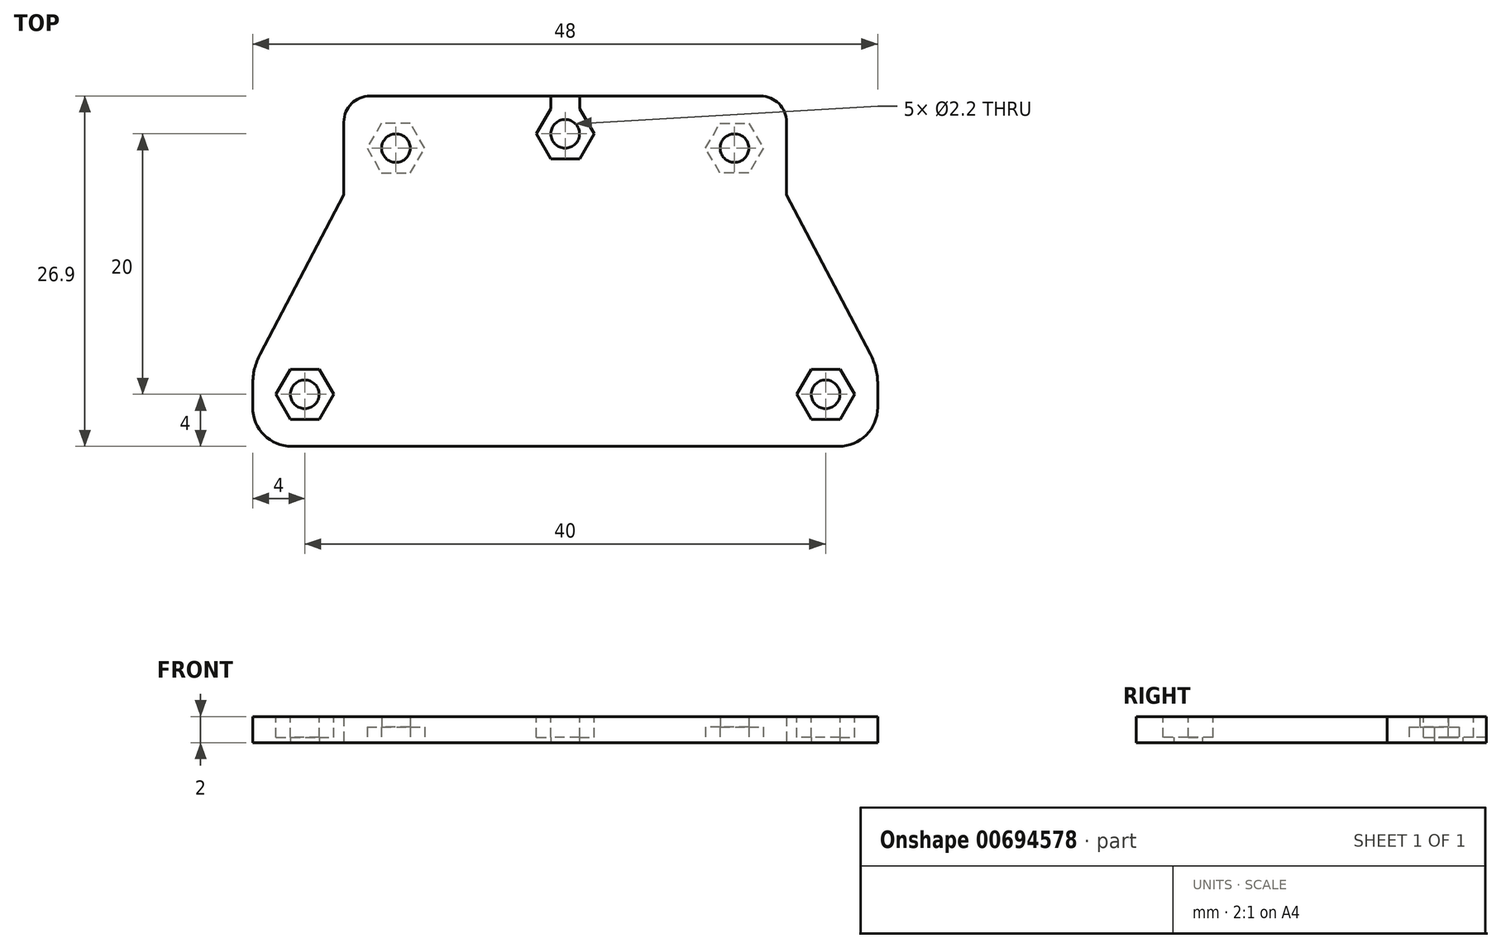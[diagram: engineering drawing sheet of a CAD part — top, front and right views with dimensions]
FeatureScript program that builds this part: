
annotation { "Feature Type Name" : "Feature", "Feature Type Description" : "" }
export const myFeature = defineFeature(function(context is Context, id is Id, definition is map)
    precondition{}
    {
        {
            var Q0;
            Q0=qCreatedBy(makeId("Top.planeOp"),FACE);
            var sketch = newSketch(context, id + "F0", { "sketchPlane" : qUnion([Q0])});
            skCircle(sketch, "E0", {"center": v(-13, 0) * mm, "radius": 1.1 * mm});
            skCircle(sketch, "E1", {"center": v(0, 1.1) * mm, "radius": 1.1 * mm});
            skCircle(sketch, "E2", {"center": v(-20, -18.9) * mm, "radius": 1.1 * mm});
            skCircle(sketch, "E3.MirrorC", {"center": v(20, -18.9) * mm, "radius": 1.1 * mm});
            skCircle(sketch, "E4.MirrorC", {"center": v(13, 0) * mm, "radius": 1.1 * mm});
            skLineSegment(sketch, "E5", {"start": v(-14.82, 3.1) * mm, "end": v(20.83, 3.1) * mm, "construction": true});
            skSolve(sketch);
        }
        {
            var Q0;
            Q0=qCreatedBy(makeId("Top.planeOp"),FACE);
            var sketch = newSketch(context, id + "F1", { "sketchPlane" : qUnion([Q0])});
            skLineSegment(sketch, "E6", {"start": v(-3, 4) * mm, "end": v(-13, 4) * mm});
            skLineSegment(sketch, "E7", {"start": v(-17, -3.6) * mm, "end": v(-24, -16.9) * mm});
            skLineSegment(sketch, "E8", {"start": v(-24, -22.9) * mm, "end": v(0, -22.9) * mm});
            skLineSegment(sketch, "E9", {"start": v(-3, 4) * mm, "end": v(0, 4) * mm});
            skLineSegment(sketch, "E10", {"start": v(-13, 4) * mm, "end": v(-17, 4) * mm});
            skLineSegment(sketch, "E11", {"start": v(-17, 4) * mm, "end": v(-17, -3.6) * mm});
            skLineSegment(sketch, "E12", {"start": v(-24, -16.9) * mm, "end": v(-24, -22.9) * mm});
            skLineSegment(sketch, "E13.MirrorCS", {"start": v(24, -22.9) * mm, "end": v(0, -22.9) * mm});
            skLineSegment(sketch, "E14.MirrorCS", {"start": v(17, -3.6) * mm, "end": v(24, -16.9) * mm});
            skLineSegment(sketch, "E15.MirrorCS", {"start": v(24, -16.9) * mm, "end": v(24, -22.9) * mm});
            skLineSegment(sketch, "E16.MirrorCS", {"start": v(3, 4) * mm, "end": v(0, 4) * mm});
            skLineSegment(sketch, "E17.MirrorCS", {"start": v(13, 4) * mm, "end": v(17, 4) * mm});
            skLineSegment(sketch, "E18.MirrorCS", {"start": v(3, 4) * mm, "end": v(13, 4) * mm});
            skLineSegment(sketch, "E19.MirrorCS", {"start": v(17, 4) * mm, "end": v(17, -3.6) * mm});
            skSolve(sketch);
        }
        {
            var Q0;
            Q0 = qSketchRegion(id + "F1", true);
            extrude(context, id + "F2", {"entities" : qUnion([Q0]), "depth" : 2 * mm, "offsetDistance" : 25 * mm});
        }
        {
            var Q0;
            Q0=makeQuery(id+"F2.opExtrude","CAP_FACE",FACE,{"disambiguationData":[OSD([sQuery(id+"F1.wireOp",EDGE,"E6"),sQuery(id+"F1.wireOp",EDGE,"E7"),sQuery(id+"F1.wireOp",EDGE,"E8"),sQuery(id+"F1.wireOp",EDGE,"E9"),sQuery(id+"F1.wireOp",EDGE,"E10"),sQuery(id+"F1.wireOp",EDGE,"E11"),sQuery(id+"F1.wireOp",EDGE,"E12"),sQuery(id+"F1.wireOp",EDGE,"E13.MirrorCS"),sQuery(id+"F1.wireOp",EDGE,"E14.MirrorCS"),sQuery(id+"F1.wireOp",EDGE,"E15.MirrorCS"),sQuery(id+"F1.wireOp",EDGE,"E16.MirrorCS"),sQuery(id+"F1.wireOp",EDGE,"E17.MirrorCS"),sQuery(id+"F1.wireOp",EDGE,"E18.MirrorCS"),sQuery(id+"F1.wireOp",EDGE,"E19.MirrorCS")])],"isStart":true});
            var sketch = newSketch(context, id + "F3", { "sketchPlane" : qUnion([Q0])});
            skCircle(sketch, "E20", {"center": v(20, 18.9) * mm, "radius": 1.1 * mm});
            skCircle(sketch, "E21", {"center": v(13, 0) * mm, "radius": 1.1 * mm});
            skCircle(sketch, "E22", {"center": v(0, -1.1) * mm, "radius": 1.1 * mm});
            skCircle(sketch, "E23", {"center": v(-13, 0) * mm, "radius": 1.1 * mm});
            skCircle(sketch, "E24", {"center": v(-20, 18.9) * mm, "radius": 1.1 * mm});
            skSolve(sketch);
        }
        {
            var Q0;
            Q0 = qSketchRegion(id + "F3", true);
            extrude(context, id + "F4", {"entities" : qUnion([Q0]), "operationType" : NewBodyOperationType.REMOVE, "endBound" : BoundingType.UP_TO_NEXT, "oppositeDirection" : true, "depth" : 25 * mm, "offsetDistance" : 25 * mm});
        }
        {
            var Q0;
            Q0=qCreatedBy(makeId("Top.planeOp"),FACE);
            var sketch = newSketch(context, id + "F5", { "sketchPlane" : qUnion([Q0])});
            skCircle(sketch, "E25.cCircle", {"center": v(13, 0) * mm, "radius": 1.92 * mm, "construction": true});
            skLineSegment(sketch, "E25.0", {"start": v(11.9, -1.92) * mm, "end": v(10.78, 0) * mm});
            skLineSegment(sketch, "E25.1", {"start": v(10.78, 0) * mm, "end": v(11.9, 1.92) * mm});
            skLineSegment(sketch, "E25.2", {"start": v(11.9, 1.92) * mm, "end": v(14.1, 1.92) * mm});
            skLineSegment(sketch, "E25.3", {"start": v(14.1, 1.92) * mm, "end": v(15.22, 0) * mm});
            skLineSegment(sketch, "E25.4", {"start": v(15.22, 0) * mm, "end": v(14.1, -1.92) * mm});
            skLineSegment(sketch, "E25.5", {"start": v(14.1, -1.92) * mm, "end": v(11.9, -1.92) * mm});
            skPoint(sketch, "E25.0.midPoint", {"position": v(11.34, -0.96) * mm});
            skLineSegment(sketch, "E26.MirrorCS", {"start": v(-11.9, -1.92) * mm, "end": v(-10.78, 0) * mm});
            skLineSegment(sketch, "E27.MirrorCS", {"start": v(-14.1, 1.92) * mm, "end": v(-15.22, 0) * mm});
            skPoint(sketch, "E28.MirrorP", {"position": v(-11.34, -0.96) * mm});
            skCircle(sketch, "E29.MirrorC", {"center": v(-13, 0) * mm, "radius": 1.92 * mm, "construction": true});
            skLineSegment(sketch, "E30.MirrorCS", {"start": v(-10.78, 0) * mm, "end": v(-11.9, 1.92) * mm});
            skLineSegment(sketch, "E31.MirrorCS", {"start": v(-11.9, 1.92) * mm, "end": v(-14.1, 1.92) * mm});
            skLineSegment(sketch, "E32.MirrorCS", {"start": v(-15.22, 0) * mm, "end": v(-14.1, -1.92) * mm});
            skLineSegment(sketch, "E33.MirrorCS", {"start": v(-14.1, -1.92) * mm, "end": v(-11.9, -1.92) * mm});
            skSolve(sketch);
        }
        {
            var Q0;
            Q0 = qSketchRegion(id + "F5", true);
            extrude(context, id + "F6", {"entities" : qUnion([Q0]), "operationType" : NewBodyOperationType.REMOVE, "depth" : 1.2 * mm, "offsetDistance" : 25 * mm});
        }
        {
            var Q0;
            Q0=makeQuery(id+"F2.opExtrude","CAP_FACE",FACE,{"disambiguationData":[OSD([sQuery(id+"F1.wireOp",EDGE,"E6"),sQuery(id+"F1.wireOp",EDGE,"E7"),sQuery(id+"F1.wireOp",EDGE,"E8"),sQuery(id+"F1.wireOp",EDGE,"E9"),sQuery(id+"F1.wireOp",EDGE,"E10"),sQuery(id+"F1.wireOp",EDGE,"E11"),sQuery(id+"F1.wireOp",EDGE,"E12"),sQuery(id+"F1.wireOp",EDGE,"E13.MirrorCS"),sQuery(id+"F1.wireOp",EDGE,"E14.MirrorCS"),sQuery(id+"F1.wireOp",EDGE,"E15.MirrorCS"),sQuery(id+"F1.wireOp",EDGE,"E16.MirrorCS"),sQuery(id+"F1.wireOp",EDGE,"E17.MirrorCS"),sQuery(id+"F1.wireOp",EDGE,"E18.MirrorCS"),sQuery(id+"F1.wireOp",EDGE,"E19.MirrorCS")])],"isStart":false});
            var sketch = newSketch(context, id + "F7", { "sketchPlane" : qUnion([Q0])});
            skCircle(sketch, "E34.cCircle", {"center": v(-20, -18.9) * mm, "radius": 1.92 * mm, "construction": true});
            skLineSegment(sketch, "E34.0", {"start": v(-18.9, -16.98) * mm, "end": v(-17.78, -18.9) * mm});
            skLineSegment(sketch, "E34.1", {"start": v(-17.78, -18.9) * mm, "end": v(-18.9, -20.82) * mm});
            skLineSegment(sketch, "E34.2", {"start": v(-18.9, -20.82) * mm, "end": v(-21.1, -20.82) * mm});
            skLineSegment(sketch, "E34.3", {"start": v(-21.1, -20.82) * mm, "end": v(-22.22, -18.9) * mm});
            skLineSegment(sketch, "E34.4", {"start": v(-22.22, -18.9) * mm, "end": v(-21.1, -16.98) * mm});
            skLineSegment(sketch, "E34.5", {"start": v(-21.1, -16.98) * mm, "end": v(-18.9, -16.98) * mm});
            skPoint(sketch, "E34.0.midPoint", {"position": v(-18.34, -17.94) * mm});
            skCircle(sketch, "E35.cCircle", {"center": v(0, 1.1) * mm, "radius": 1.92 * mm, "construction": true});
            skLineSegment(sketch, "E35.0", {"start": v(-1.1, 3.02) * mm, "end": v(1.1, 3.02) * mm});
            skLineSegment(sketch, "E35.1", {"start": v(1.1, 3.02) * mm, "end": v(2.22, 1.1) * mm});
            skLineSegment(sketch, "E35.2", {"start": v(2.22, 1.1) * mm, "end": v(1.1, -0.82) * mm});
            skLineSegment(sketch, "E35.3", {"start": v(1.1, -0.82) * mm, "end": v(-1.1, -0.82) * mm});
            skLineSegment(sketch, "E35.4", {"start": v(-1.1, -0.82) * mm, "end": v(-2.22, 1.1) * mm});
            skLineSegment(sketch, "E35.5", {"start": v(-2.22, 1.1) * mm, "end": v(-1.1, 3.02) * mm});
            skPoint(sketch, "E35.0.midPoint", {"position": v(0, 3.02) * mm});
            skLineSegment(sketch, "E36.MirrorCS", {"start": v(17.78, -18.9) * mm, "end": v(18.9, -20.82) * mm});
            skLineSegment(sketch, "E37.MirrorCS", {"start": v(22.22, -18.9) * mm, "end": v(21.1, -16.98) * mm});
            skLineSegment(sketch, "E38.MirrorCS", {"start": v(18.9, -16.98) * mm, "end": v(17.78, -18.9) * mm});
            skLineSegment(sketch, "E39.MirrorCS", {"start": v(21.1, -20.82) * mm, "end": v(22.22, -18.9) * mm});
            skLineSegment(sketch, "E40.MirrorCS", {"start": v(21.1, -16.98) * mm, "end": v(18.9, -16.98) * mm});
            skCircle(sketch, "E41.MirrorC", {"center": v(20, -18.9) * mm, "radius": 1.92 * mm, "construction": true});
            skLineSegment(sketch, "E42.MirrorCS", {"start": v(18.9, -20.82) * mm, "end": v(21.1, -20.82) * mm});
            skPoint(sketch, "E43.MirrorP", {"position": v(18.34, -17.94) * mm});
            skLineSegment(sketch, "E44", {"start": v(-1.1, 3.02) * mm, "end": v(-1.1, 4) * mm});
            skLineSegment(sketch, "E45", {"start": v(-1.1, 4) * mm, "end": v(1.1, 4) * mm});
            skLineSegment(sketch, "E46", {"start": v(1.1, 4) * mm, "end": v(1.1, 3.02) * mm});
            skSolve(sketch);
        }
        {
            var Q0;
            Q0 = qSketchRegion(id + "F7", true);
            var Q1;
            Q1 = qConstructionFilter(qBodyType(qCreatedBy(id + "F7" ,EDGE), BodyType.WIRE), ConstructionObject.NO);
            extrude(context, id + "F8", {"entities" : qUnion([Q0]), "operationType" : NewBodyOperationType.REMOVE, "surfaceEntities" : qUnion([Q1]), "oppositeDirection" : true, "depth" : 1.6 * mm, "offsetDistance" : 25 * mm});
        }
        {
            var Q0;
            Q0=makeQuery(id+"F2.opExtrude","SWEPT_EDGE",EDGE,{"disambiguationData":[OSD([sQuery(id+"F1.wireOp",EDGE,"E10"),sQuery(id+"F1.wireOp",EDGE,"E11")])]});
            var Q1;
            Q1=makeQuery(id+"F2.opExtrude","SWEPT_EDGE",EDGE,{"disambiguationData":[OSD([sQuery(id+"F1.wireOp",EDGE,"E17.MirrorCS"),sQuery(id+"F1.wireOp",EDGE,"E19.MirrorCS")])]});
            fillet(context, id + "F9", {"entities" : qUnion([Q0, Q1]), "radius" : 2 * mm, "tangentPropagation" : true, "allowEdgeOverflow" : false});
        }
        {
            var Q0;
            Q0=makeQuery(id+"F2.opExtrude","SWEPT_EDGE",EDGE,{"disambiguationData":[OSD([sQuery(id+"F1.wireOp",EDGE,"E14.MirrorCS"),sQuery(id+"F1.wireOp",EDGE,"E15.MirrorCS")])]});
            var Q1;
            Q1=makeQuery(id+"F2.opExtrude","SWEPT_EDGE",EDGE,{"disambiguationData":[OSD([sQuery(id+"F1.wireOp",EDGE,"E7"),sQuery(id+"F1.wireOp",EDGE,"E12")])]});
            var Q2;
            Q2=makeQuery(id+"F2.opExtrude","SWEPT_EDGE",EDGE,{"disambiguationData":[OSD([sQuery(id+"F1.wireOp",EDGE,"E6"),sQuery(id+"F1.wireOp",EDGE,"E9")])]});
            var Q3;
            Q3=makeQuery(id+"F2.opExtrude","SWEPT_EDGE",EDGE,{"disambiguationData":[OSD([sQuery(id+"F1.wireOp",EDGE,"E16.MirrorCS"),sQuery(id+"F1.wireOp",EDGE,"E18.MirrorCS")])]});
            fillet(context, id + "F10", {"entities" : qUnion([Q0, Q1, Q2, Q3]), "radius" : 5 * mm, "tangentPropagation" : true, "allowEdgeOverflow" : false});
        }
        {
            var Q0;
            Q0=makeQuery(id+"F2.opExtrude","SWEPT_EDGE",EDGE,{"disambiguationData":[OSD([sQuery(id+"F1.wireOp",EDGE,"E13.MirrorCS"),sQuery(id+"F1.wireOp",EDGE,"E15.MirrorCS")])]});
            var Q1;
            Q1=makeQuery(id+"F2.opExtrude","SWEPT_EDGE",EDGE,{"disambiguationData":[OSD([sQuery(id+"F1.wireOp",EDGE,"E8"),sQuery(id+"F1.wireOp",EDGE,"E12")])]});
            fillet(context, id + "F11", {"entities" : qUnion([Q0, Q1]), "radius" : 3 * mm, "tangentPropagation" : true, "allowEdgeOverflow" : false});
        }
    });
